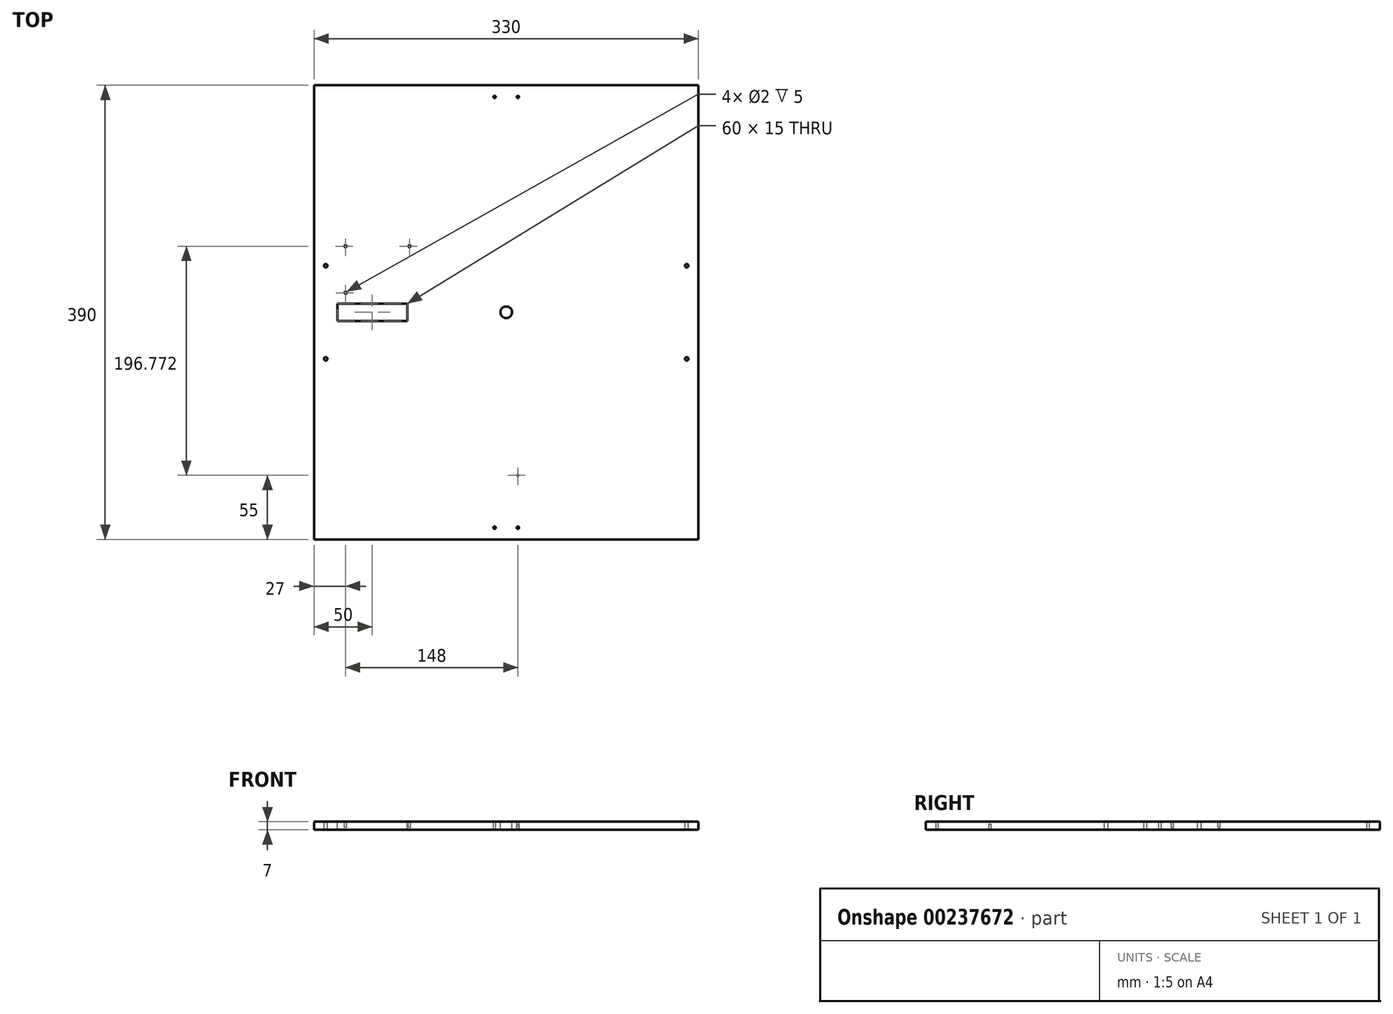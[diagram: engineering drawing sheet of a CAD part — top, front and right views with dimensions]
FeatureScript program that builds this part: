
annotation { "Feature Type Name" : "Feature", "Feature Type Description" : "" }
export const myFeature = defineFeature(function(context is Context, id is Id, definition is map)
    precondition{}
    {
        {
            var Q0;
            Q0=qCreatedBy(makeId("Top.planeOp"),FACE);
            var sketch = newSketch(context, id + "F0", { "sketchPlane" : qUnion([Q0])});
            skLineSegment(sketch, "E0.bottom", {"start": v(-165, -195) * mm, "end": v(165, -195) * mm});
            skLineSegment(sketch, "E0.top", {"start": v(-165, 195) * mm, "end": v(165, 195) * mm});
            skLineSegment(sketch, "E0.left", {"start": v(-165, -195) * mm, "end": v(-165, 195) * mm});
            skLineSegment(sketch, "E0.right", {"start": v(165, -195) * mm, "end": v(165, 195) * mm});
            skPoint(sketch, "E0.middle", {"position": v(0, 0) * mm});
            skSolve(sketch);
        }
        {
            var Q0;
            Q0 = qSketchRegion(id + "F0", true);
            extrude(context, id + "F1", {"entities" : qUnion([Q0]), "depth" : 7 * mm});
        }
        {
            var Q0;
            Q0=makeQuery(id+"F1.opExtrude","CAP_FACE",FACE,{"disambiguationData":[OSD([sQuery(id+"F0.wireOp",EDGE,"E0.bottom"),sQuery(id+"F0.wireOp",EDGE,"E0.top"),sQuery(id+"F0.wireOp",EDGE,"E0.left"),sQuery(id+"F0.wireOp",EDGE,"E0.right")])],"isStart":false});
            var sketch = newSketch(context, id + "F2", { "sketchPlane" : qUnion([Q0])});
            skCircle(sketch, "E1", {"center": v(-155, 40) * mm, "radius": 1.5 * mm});
            skCircle(sketch, "E2", {"center": v(-155, -40) * mm, "radius": 1.5 * mm});
            skSolve(sketch);
        }
        {
            var Q0;
            Q0 = qSketchRegion(id + "F2", true);
            extrude(context, id + "F3", {"entities" : qUnion([Q0]), "operationType" : NewBodyOperationType.REMOVE, "oppositeDirection" : true, "depth" : 25 * mm});
        }
        {
            var Q0;
            Q0=makeQuery(id+"F1.opExtrude","CAP_FACE",FACE,{"disambiguationData":[OSD([sQuery(id+"F0.wireOp",EDGE,"E0.bottom"),sQuery(id+"F0.wireOp",EDGE,"E0.top"),sQuery(id+"F0.wireOp",EDGE,"E0.left"),sQuery(id+"F0.wireOp",EDGE,"E0.right")])],"isStart":false});
            var sketch = newSketch(context, id + "F4", { "sketchPlane" : qUnion([Q0])});
            skLineSegment(sketch, "E3", {"start": v(165, 195) * mm, "end": v(165, 30) * mm});
            skPoint(sketch, "E4.endSnap0", {"position": v(155, 20) * mm});
            skCircle(sketch, "E5", {"center": v(155, 40) * mm, "radius": 1.5 * mm});
            skCircle(sketch, "E6", {"center": v(155, -40) * mm, "radius": 1.5 * mm});
            skSolve(sketch);
        }
        {
            var Q0;
            Q0 = qSketchRegion(id + "F4", true);
            extrude(context, id + "F5", {"entities" : qUnion([Q0]), "operationType" : NewBodyOperationType.REMOVE, "oppositeDirection" : true, "depth" : 25 * mm});
        }
        {
            var Q0;
            Q0=makeQuery(id+"F1.opExtrude","CAP_FACE",FACE,{"disambiguationData":[OSD([sQuery(id+"F0.wireOp",EDGE,"E0.bottom"),sQuery(id+"F0.wireOp",EDGE,"E0.top"),sQuery(id+"F0.wireOp",EDGE,"E0.left"),sQuery(id+"F0.wireOp",EDGE,"E0.right")])],"isStart":false});
            var sketch = newSketch(context, id + "F6", { "sketchPlane" : qUnion([Q0])});
            skCircle(sketch, "E7", {"center": v(-138, 56.77) * mm, "radius": 1 * mm});
            skCircle(sketch, "E8", {"center": v(-83, 56.77) * mm, "radius": 1 * mm});
            skCircle(sketch, "E9", {"center": v(-137.85, 16.77) * mm, "radius": 1 * mm});
            skLineSegment(sketch, "E10", {"start": v(-165, 16.77) * mm, "end": v(-138, 16.77) * mm});
            skLineSegment(sketch, "E11", {"start": v(-138, 16.77) * mm, "end": v(-138, 56.77) * mm});
            skLineSegment(sketch, "E12", {"start": v(-138, 56.77) * mm, "end": v(-83, 56.77) * mm});
            skSolve(sketch);
        }
        {
            var Q0;
            Q0 = qSketchRegion(id + "F6", true);
            extrude(context, id + "F7", {"entities" : qUnion([Q0]), "operationType" : NewBodyOperationType.REMOVE, "oppositeDirection" : true, "depth" : 5 * mm});
        }
        {
            var Q0;
            Q0=makeQuery(id+"F1.opExtrude","CAP_FACE",FACE,{"disambiguationData":[OSD([sQuery(id+"F0.wireOp",EDGE,"E0.bottom"),sQuery(id+"F0.wireOp",EDGE,"E0.top"),sQuery(id+"F0.wireOp",EDGE,"E0.left"),sQuery(id+"F0.wireOp",EDGE,"E0.right")])],"isStart":false});
            var sketch = newSketch(context, id + "F8", { "sketchPlane" : qUnion([Q0])});
            skLineSegment(sketch, "E13", {"start": v(-145, 0) * mm, "end": v(-145, -7.5) * mm});
            skLineSegment(sketch, "E14", {"start": v(-145, -7.5) * mm, "end": v(-85, -7.5) * mm});
            skLineSegment(sketch, "E15", {"start": v(-85, -7.5) * mm, "end": v(-85, 7.5) * mm});
            skLineSegment(sketch, "E16", {"start": v(-85, 7.5) * mm, "end": v(-145, 7.5) * mm});
            skLineSegment(sketch, "E17", {"start": v(-145, 7.5) * mm, "end": v(-145, 0) * mm});
            skSolve(sketch);
        }
        {
            var Q0;
            Q0 = qSketchRegion(id + "F8", true);
            extrude(context, id + "F9", {"entities" : qUnion([Q0]), "operationType" : NewBodyOperationType.REMOVE, "oppositeDirection" : true, "depth" : 25 * mm});
        }
        {
            var Q0;
            Q0=makeQuery(id+"F1.opExtrude","CAP_FACE",FACE,{"disambiguationData":[OSD([sQuery(id+"F0.wireOp",EDGE,"E0.bottom"),sQuery(id+"F0.wireOp",EDGE,"E0.top"),sQuery(id+"F0.wireOp",EDGE,"E0.left"),sQuery(id+"F0.wireOp",EDGE,"E0.right")])],"isStart":false});
            var sketch = newSketch(context, id + "F10", { "sketchPlane" : qUnion([Q0])});
            skCircle(sketch, "E18", {"center": v(0, 0) * mm, "radius": 5 * mm});
            skSolve(sketch);
        }
        {
            var Q0;
            Q0 = qSketchRegion(id + "F10", true);
            extrude(context, id + "F11", {"entities" : qUnion([Q0]), "operationType" : NewBodyOperationType.REMOVE, "oppositeDirection" : true, "depth" : 25 * mm});
        }
        {
            var Q0;
            Q0=makeQuery(id+"F1.opExtrude","CAP_FACE",FACE,{"disambiguationData":[OSD([sQuery(id+"F0.wireOp",EDGE,"E0.bottom"),sQuery(id+"F0.wireOp",EDGE,"E0.top"),sQuery(id+"F0.wireOp",EDGE,"E0.left"),sQuery(id+"F0.wireOp",EDGE,"E0.right")])],"isStart":false});
            var sketch = newSketch(context, id + "F12", { "sketchPlane" : qUnion([Q0])});
            skCircle(sketch, "E19", {"center": v(10, 185) * mm, "radius": 1 * mm});
            skCircle(sketch, "E20", {"center": v(-10, 185) * mm, "radius": 1 * mm});
            skCircle(sketch, "E21", {"center": v(10, -185) * mm, "radius": 1 * mm});
            skCircle(sketch, "E22", {"center": v(-10, -185) * mm, "radius": 1 * mm});
            skSolve(sketch);
        }
        {
            var Q0;
            Q0 = qSketchRegion(id + "F12", true);
            extrude(context, id + "F13", {"entities" : qUnion([Q0]), "operationType" : NewBodyOperationType.REMOVE, "oppositeDirection" : true, "depth" : 50 * mm});
        }
        {
            var Q0;
            Q0=makeQuery(id+"F1.opExtrude","CAP_FACE",FACE,{"disambiguationData":[OSD([sQuery(id+"F0.wireOp",EDGE,"E0.bottom"),sQuery(id+"F0.wireOp",EDGE,"E0.top"),sQuery(id+"F0.wireOp",EDGE,"E0.left"),sQuery(id+"F0.wireOp",EDGE,"E0.right")])],"isStart":true});
            var sketch = newSketch(context, id + "F14", { "sketchPlane" : qUnion([Q0])});
            skCircle(sketch, "E23", {"center": v(10, 140) * mm, "radius": 1 * mm});
            skSolve(sketch);
        }
        {
            var Q0;
            Q0 = qSketchRegion(id + "F14", true);
            extrude(context, id + "F15", {"entities" : qUnion([Q0]), "operationType" : NewBodyOperationType.REMOVE, "oppositeDirection" : true, "depth" : 5 * mm});
        }
    });
